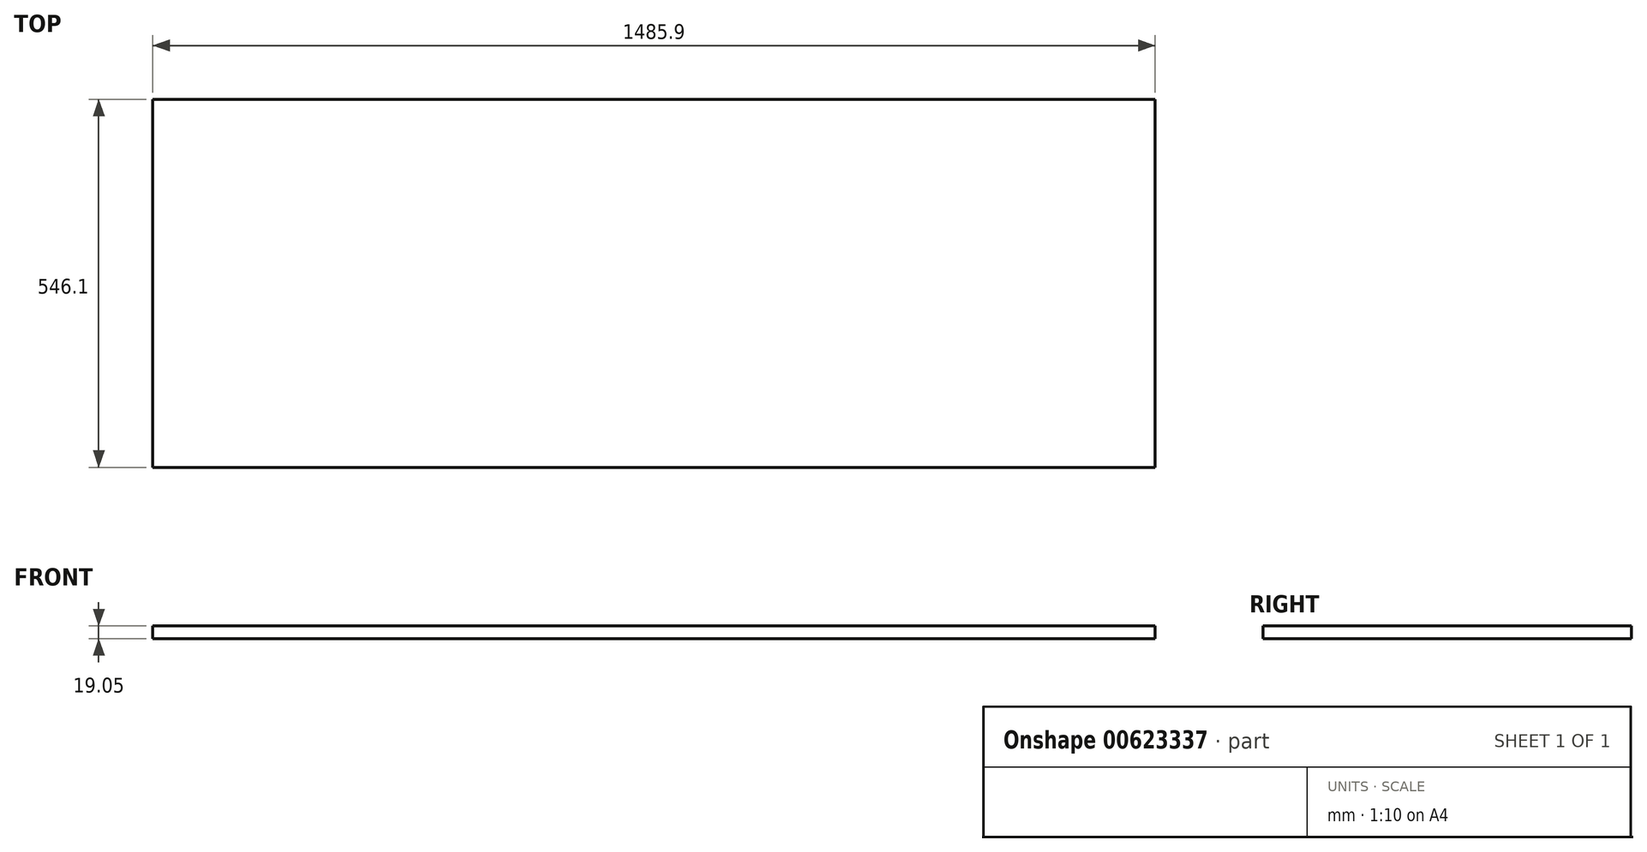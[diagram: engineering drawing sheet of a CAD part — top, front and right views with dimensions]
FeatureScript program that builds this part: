
annotation { "Feature Type Name" : "Feature", "Feature Type Description" : "" }
export const myFeature = defineFeature(function(context is Context, id is Id, definition is map)
    precondition{}
    {
        {
            var Q0;
            Q0=qCreatedBy(makeId("Top.planeOp"),FACE);
            var sketch = newSketch(context, id + "F0", { "sketchPlane" : qUnion([Q0])});
            skLineSegment(sketch, "E0.bottom", {"start": v(-742.95, 273.05) * mm, "end": v(742.95, 273.05) * mm});
            skLineSegment(sketch, "E0.top", {"start": v(-742.95, -273.05) * mm, "end": v(742.95, -273.05) * mm});
            skLineSegment(sketch, "E0.left", {"start": v(-742.95, 273.05) * mm, "end": v(-742.95, -273.05) * mm});
            skLineSegment(sketch, "E0.right", {"start": v(742.95, 273.05) * mm, "end": v(742.95, -273.05) * mm});
            skPoint(sketch, "E0.middle", {"position": v(0, 0) * mm});
            skSolve(sketch);
        }
        {
            var Q0;
            Q0=makeQuery(id+"F0.imprint","IMPRINT",FACE,{"disambiguationData":[TD([[makeQuery(id+"F0.imprint","IMPRINT",EDGE,{"derivedFrom":sQuery(id+"F0.wireOp",EDGE,"E0.bottom")}),-1.0]])]});
            extrude(context, id + "F1", {"entities" : qUnion([Q0]), "depth" : 19.05 * mm, "offsetDistance" : 25.4 * mm});
        }
    });
